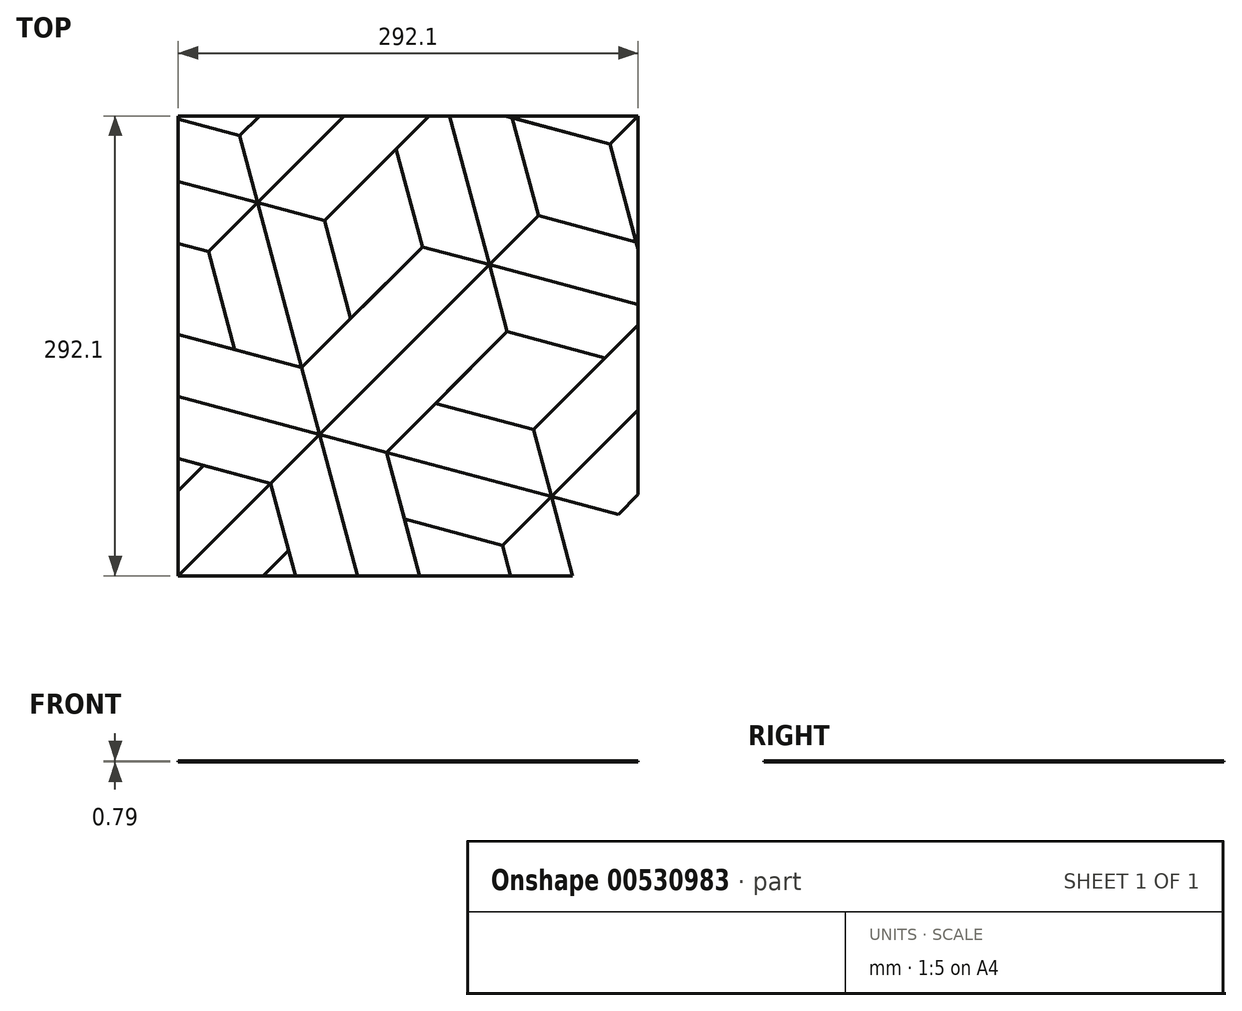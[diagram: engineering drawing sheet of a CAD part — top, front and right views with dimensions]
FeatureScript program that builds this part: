
annotation { "Feature Type Name" : "Feature", "Feature Type Description" : "" }
export const myFeature = defineFeature(function(context is Context, id is Id, definition is map)
    precondition{}
    {
        {
            var Q0;
            Q0=qCreatedBy(makeId("Top.planeOp"),FACE);
            var sketch = newSketch(context, id + "F0", { "sketchPlane" : qUnion([Q0])});
            skLineSegment(sketch, "E0.bottom", {"start": v(146.05, 146.05) * mm, "end": v(-146.05, 146.05) * mm});
            skLineSegment(sketch, "E0.top", {"start": v(146.05, -146.05) * mm, "end": v(-146.05, -146.05) * mm});
            skLineSegment(sketch, "E0.left", {"start": v(146.05, 146.05) * mm, "end": v(146.05, -146.05) * mm});
            skLineSegment(sketch, "E0.right", {"start": v(-146.05, 146.05) * mm, "end": v(-146.05, -146.05) * mm});
            skPoint(sketch, "E0.middle", {"position": v(0, 0) * mm});
            skLineSegment(sketch, "E1", {"start": v(-146.05, -146.05) * mm, "end": v(82.62, 82.62) * mm});
            skPoint(sketch, "E2", {"position": v(51.52, 51.52) * mm});
            skLineSegment(sketch, "E3", {"start": v(104.45, -146.05) * mm, "end": v(79.57, -53.2) * mm});
            skLineSegment(sketch, "E4", {"start": v(146.05, 26.19) * mm, "end": v(9.02, 62.9) * mm});
            skLineSegment(sketch, "E5", {"start": v(82.62, 82.62) * mm, "end": v(65.95, 144.84) * mm});
            skPoint(sketch, "E5.endSnap0", {"position": v(0, 146.05) * mm});
            skLineSegment(sketch, "E6", {"start": v(9.02, 62.9) * mm, "end": v(-7.65, 125.12) * mm});
            skLineSegment(sketch, "E7", {"start": v(82.62, 82.62) * mm, "end": v(144.84, 65.95) * mm});
            skLineSegment(sketch, "E8", {"start": v(62.9, 9.02) * mm, "end": v(125.12, -7.65) * mm});
            skLineSegment(sketch, "E9", {"start": v(62.9, 9.02) * mm, "end": v(-13.75, -67.63) * mm});
            skLineSegment(sketch, "E10", {"start": v(9.02, 62.9) * mm, "end": v(-67.63, -13.75) * mm});
            skPoint(sketch, "E11", {"position": v(-95.7, 90.96) * mm});
            skLineSegment(sketch, "E12", {"start": v(-107.08, 133.45) * mm, "end": v(-32.18, -146.05) * mm});
            skLineSegment(sketch, "E13", {"start": v(-126.8, 59.85) * mm, "end": v(-40.6, 146.05) * mm});
            skLineSegment(sketch, "E14", {"start": v(-53.2, 79.57) * mm, "end": v(-36.53, 17.36) * mm});
            skLineSegment(sketch, "E15", {"start": v(-53.2, 79.57) * mm, "end": v(13.28, 146.05) * mm});
            skLineSegment(sketch, "E16", {"start": v(-126.8, 59.85) * mm, "end": v(-110.13, -2.37) * mm});
            skLineSegment(sketch, "E17", {"start": v(-126.8, 59.85) * mm, "end": v(-146.05, 65) * mm});
            skLineSegment(sketch, "E18", {"start": v(-107.08, 133.45) * mm, "end": v(-94.48, 146.05) * mm});
            skLineSegment(sketch, "E19", {"start": v(-107.08, 133.45) * mm, "end": v(-146.05, 143.9) * mm});
            skLineSegment(sketch, "E20", {"start": v(-146.05, -32.18) * mm, "end": v(133.45, -107.08) * mm});
            skPoint(sketch, "E21", {"position": v(-13.75, -67.63) * mm});
            skLineSegment(sketch, "E22", {"start": v(-146.05, 7.26) * mm, "end": v(-67.63, -13.75) * mm});
            skLineSegment(sketch, "E23", {"start": v(-146.05, -71.63) * mm, "end": v(-87.36, -87.36) * mm});
            skLineSegment(sketch, "E24", {"start": v(59.85, -126.8) * mm, "end": v(146.05, -40.6) * mm});
            skLineSegment(sketch, "E25", {"start": v(79.57, -53.2) * mm, "end": v(146.05, 13.28) * mm});
            skLineSegment(sketch, "E26", {"start": v(59.85, -126.8) * mm, "end": v(65, -146.05) * mm});
            skLineSegment(sketch, "E27", {"start": v(133.45, -107.08) * mm, "end": v(143.9, -146.05) * mm});
            skLineSegment(sketch, "E28", {"start": v(143.9, -146.05) * mm, "end": v(133.45, -107.08) * mm});
            skLineSegment(sketch, "E29", {"start": v(133.45, -107.08) * mm, "end": v(146.05, -94.48) * mm});
            skLineSegment(sketch, "E30.trimOffspring", {"start": v(-13.75, -67.63) * mm, "end": v(7.26, -146.05) * mm});
            skLineSegment(sketch, "E31.trimOffspring", {"start": v(17.36, -36.53) * mm, "end": v(79.57, -53.2) * mm});
            skLineSegment(sketch, "E32.trimOffspring", {"start": v(-75.97, -129.85) * mm, "end": v(-92.17, -146.05) * mm});
            skLineSegment(sketch, "E33.trimOffspring", {"start": v(-2.37, -110.13) * mm, "end": v(59.85, -126.8) * mm});
            skLineSegment(sketch, "E34.trimOffspring", {"start": v(-129.85, -75.97) * mm, "end": v(-146.05, -92.17) * mm});
            skLineSegment(sketch, "E35.trimOffspring", {"start": v(-87.36, -87.36) * mm, "end": v(-71.63, -146.05) * mm});
            skLineSegment(sketch, "E36.trimOffspring", {"start": v(-53.2, 79.57) * mm, "end": v(-146.05, 104.45) * mm});
            skLineSegment(sketch, "E37.trimOffspring", {"start": v(62.9, 9.02) * mm, "end": v(26.19, 146.05) * mm});
            skLineSegment(sketch, "E38", {"start": v(61.44, 146.05) * mm, "end": v(128.17, 128.17) * mm});
            skLineSegment(sketch, "E39", {"start": v(128.17, 128.17) * mm, "end": v(146.05, 61.44) * mm});
            skLineSegment(sketch, "E40.trimOffspring", {"start": v(128.17, 128.17) * mm, "end": v(146.05, 146.05) * mm});
            skPoint(sketch, "E41.orphan", {"position": v(65.63, 146.05) * mm});
            skSolve(sketch);
        }
        {
            var Q0;
            {var subQ2=sQuery(id+"F0.wireOp",EDGE,"E0.bottom");var subQ6=sQuery(id+"F0.wireOp",EDGE,"E13");var subQ7=makeQuery(id+"F0.imprint","INTERSECT",VERTEX,{"derivedFrom":[subQ2,subQ6]});Q0=makeQuery(id+"F0.imprint","IMPRINT",FACE,{"disambiguationData":[TD([[makeQuery(id+"F0.imprint","IMPRINT",EDGE,{"disambiguationData":[TD([[subQ7,1.0]])],"derivedFrom":subQ2}),1.0]])]});}
            var Q1;
            {var subQ5=sQuery(id+"F0.wireOp",EDGE,"E16");Q1=makeQuery(id+"F0.imprint","IMPRINT",FACE,{"disambiguationData":[TD([[makeQuery(id+"F0.imprint","IMPRINT",EDGE,{"derivedFrom":subQ5}),1.0]])]});}
            var Q2;
            {var subQ0=sQuery(id+"F0.wireOp",EDGE,"E19");Q2=makeQuery(id+"F0.imprint","IMPRINT",FACE,{"disambiguationData":[TD([[makeQuery(id+"F0.imprint","IMPRINT",EDGE,{"derivedFrom":subQ0}),1.0]])]});}
            var Q3;
            {var subQ3=sQuery(id+"F0.wireOp",EDGE,"E32.trimOffspring");Q3=makeQuery(id+"F0.imprint","IMPRINT",FACE,{"disambiguationData":[TD([[makeQuery(id+"F0.imprint","IMPRINT",EDGE,{"derivedFrom":subQ3}),-1.0]])]});}
            var Q4;
            {var subQ0=sQuery(id+"F0.wireOp",EDGE,"E31.trimOffspring");Q4=makeQuery(id+"F0.imprint","IMPRINT",FACE,{"disambiguationData":[TD([[makeQuery(id+"F0.imprint","IMPRINT",EDGE,{"derivedFrom":subQ0}),-1.0]])]});}
            var Q5;
            {var subQ3=sQuery(id+"F0.wireOp",EDGE,"E29");Q5=makeQuery(id+"F0.imprint","IMPRINT",FACE,{"disambiguationData":[TD([[makeQuery(id+"F0.imprint","IMPRINT",EDGE,{"derivedFrom":subQ3}),1.0]])]});}
            var Q6;
            {var subQ3=sQuery(id+"F0.wireOp",EDGE,"E26");Q6=makeQuery(id+"F0.imprint","IMPRINT",FACE,{"disambiguationData":[TD([[makeQuery(id+"F0.imprint","IMPRINT",EDGE,{"derivedFrom":subQ3}),1.0]])]});}
            var Q7;
            {var subQ1=sQuery(id+"F0.wireOp",EDGE,"E10");var subQ3=makeQuery(id+"F0.imprint","INTERSECT",VERTEX,{"derivedFrom":[subQ1,sQuery(id+"F0.wireOp",EDGE,"E14")]});Q7=makeQuery(id+"F0.imprint","IMPRINT",FACE,{"disambiguationData":[TD([[makeQuery(id+"F0.imprint","IMPRINT",EDGE,{"disambiguationData":[TD([[subQ3,1.0]])],"derivedFrom":subQ1}),1.0]])]});}
            var Q8;
            {var subQ3=sQuery(id+"F0.wireOp",EDGE,"E12");var subQ5=sQuery(id+"F0.wireOp",EDGE,"E0.top");var subQ6=makeQuery(id+"F0.imprint","INTERSECT",VERTEX,{"derivedFrom":[subQ5,subQ3]});Q8=makeQuery(id+"F0.imprint","IMPRINT",FACE,{"disambiguationData":[TD([[makeQuery(id+"F0.imprint","IMPRINT",EDGE,{"disambiguationData":[TD([[subQ6,1.0]])],"derivedFrom":subQ5}),-1.0]])]});}
            var Q9;
            {var subQ1=sQuery(id+"F0.wireOp",EDGE,"E0.right");var subQ4=sQuery(id+"F0.wireOp",EDGE,"E20");var subQ5=makeQuery(id+"F0.imprint","INTERSECT",VERTEX,{"derivedFrom":[subQ1,subQ4]});Q9=makeQuery(id+"F0.imprint","IMPRINT",FACE,{"disambiguationData":[TD([[makeQuery(id+"F0.imprint","IMPRINT",EDGE,{"disambiguationData":[TD([[subQ5,-1.0]])],"derivedFrom":subQ1}),1.0]])]});}
            var Q10;
            {var subQ1=sQuery(id+"F0.wireOp",EDGE,"E8");Q10=makeQuery(id+"F0.imprint","IMPRINT",FACE,{"disambiguationData":[TD([[makeQuery(id+"F0.imprint","IMPRINT",EDGE,{"derivedFrom":subQ1}),1.0]])]});}
            var Q11;
            {var subQ5=sQuery(id+"F0.wireOp",EDGE,"E5");Q11=makeQuery(id+"F0.imprint","IMPRINT",FACE,{"disambiguationData":[TD([[makeQuery(id+"F0.imprint","IMPRINT",EDGE,{"derivedFrom":subQ5}),1.0]])]});}
            var Q12;
            {var subQ0=sQuery(id+"F0.wireOp",EDGE,"E40.trimOffspring");Q12=makeQuery(id+"F0.imprint","IMPRINT",FACE,{"disambiguationData":[TD([[makeQuery(id+"F0.imprint","IMPRINT",EDGE,{"derivedFrom":subQ0}),-1.0]])]});}
            extrude(context, id + "F1", {"entities" : qUnion([Q0, Q1, Q2, Q3, Q4, Q5, Q6, Q7, Q8, Q9, Q10, Q11, Q12]), "depth" : 0.8 * mm, "offsetDistance" : 25.4 * mm});
        }
        {
            var Q0;
            {var subQ3=sQuery(id+"F0.wireOp",EDGE,"E18");Q0=makeQuery(id+"F0.imprint","IMPRINT",FACE,{"disambiguationData":[TD([[makeQuery(id+"F0.imprint","IMPRINT",EDGE,{"derivedFrom":subQ3}),-1.0]])]});}
            var Q1;
            {var subQ0=sQuery(id+"F0.wireOp",EDGE,"E17");Q1=makeQuery(id+"F0.imprint","IMPRINT",FACE,{"disambiguationData":[TD([[makeQuery(id+"F0.imprint","IMPRINT",EDGE,{"derivedFrom":subQ0}),-1.0]])]});}
            var Q2;
            {var subQ3=sQuery(id+"F0.wireOp",EDGE,"E14");Q2=makeQuery(id+"F0.imprint","IMPRINT",FACE,{"disambiguationData":[TD([[makeQuery(id+"F0.imprint","IMPRINT",EDGE,{"derivedFrom":subQ3}),-1.0]])]});}
            var Q3;
            {var subQ0=sQuery(id+"F0.wireOp",EDGE,"E20");var subQ1=sQuery(id+"F0.wireOp",EDGE,"E0.right");var subQ2=makeQuery(id+"F0.imprint","INTERSECT",VERTEX,{"derivedFrom":[subQ1,subQ0]});Q3=makeQuery(id+"F0.imprint","IMPRINT",FACE,{"disambiguationData":[TD([[makeQuery(id+"F0.imprint","IMPRINT",EDGE,{"disambiguationData":[TD([[subQ2,1.0]])],"derivedFrom":subQ1}),1.0]])]});}
            var Q4;
            {var subQ3=sQuery(id+"F0.wireOp",EDGE,"E34.trimOffspring");Q4=makeQuery(id+"F0.imprint","IMPRINT",FACE,{"disambiguationData":[TD([[makeQuery(id+"F0.imprint","IMPRINT",EDGE,{"derivedFrom":subQ3}),1.0]])]});}
            var Q5;
            {var subQ4=sQuery(id+"F0.wireOp",EDGE,"E12");var subQ5=sQuery(id+"F0.wireOp",EDGE,"E0.top");var subQ6=makeQuery(id+"F0.imprint","INTERSECT",VERTEX,{"derivedFrom":[subQ5,subQ4]});Q5=makeQuery(id+"F0.imprint","IMPRINT",FACE,{"disambiguationData":[TD([[makeQuery(id+"F0.imprint","IMPRINT",EDGE,{"disambiguationData":[TD([[subQ6,-1.0]])],"derivedFrom":subQ5}),-1.0]])]});}
            var Q6;
            {var subQ1=sQuery(id+"F0.wireOp",EDGE,"E9");var subQ5=makeQuery(id+"F0.imprint","INTERSECT",VERTEX,{"derivedFrom":[subQ1,sQuery(id+"F0.wireOp",EDGE,"E31.trimOffspring")]});Q6=makeQuery(id+"F0.imprint","IMPRINT",FACE,{"disambiguationData":[TD([[makeQuery(id+"F0.imprint","IMPRINT",EDGE,{"disambiguationData":[TD([[subQ5,1.0]])],"derivedFrom":subQ1}),-1.0]])]});}
            var Q7;
            {var subQ5=sQuery(id+"F0.wireOp",EDGE,"E33.trimOffspring");Q7=makeQuery(id+"F0.imprint","IMPRINT",FACE,{"disambiguationData":[TD([[makeQuery(id+"F0.imprint","IMPRINT",EDGE,{"derivedFrom":subQ5}),1.0]])]});}
            var Q8;
            {var subQ3=sQuery(id+"F0.wireOp",EDGE,"E28");Q8=makeQuery(id+"F0.imprint","IMPRINT",FACE,{"disambiguationData":[TD([[makeQuery(id+"F0.imprint","IMPRINT",EDGE,{"derivedFrom":subQ3}),1.0]])]});}
            var Q9;
            {var subQ0=sQuery(id+"F0.wireOp",EDGE,"E24");var subQ1=sQuery(id+"F0.wireOp",EDGE,"E0.left");var subQ2=makeQuery(id+"F0.imprint","INTERSECT",VERTEX,{"derivedFrom":[subQ1,subQ0]});Q9=makeQuery(id+"F0.imprint","IMPRINT",FACE,{"disambiguationData":[TD([[makeQuery(id+"F0.imprint","IMPRINT",EDGE,{"disambiguationData":[TD([[subQ2,1.0]])],"derivedFrom":subQ1}),-1.0]])]});}
            var Q10;
            {var subQ0=sQuery(id+"F0.wireOp",EDGE,"E7");Q10=makeQuery(id+"F0.imprint","IMPRINT",FACE,{"disambiguationData":[TD([[makeQuery(id+"F0.imprint","IMPRINT",EDGE,{"derivedFrom":subQ0}),-1.0]])]});}
            var Q11;
            {var subQ0=sQuery(id+"F0.wireOp",EDGE,"E6");Q11=makeQuery(id+"F0.imprint","IMPRINT",FACE,{"disambiguationData":[TD([[makeQuery(id+"F0.imprint","IMPRINT",EDGE,{"derivedFrom":subQ0}),-1.0]])]});}
            var Q12;
            {var subQ0=sQuery(id+"F0.wireOp",EDGE,"E40.trimOffspring");Q12=makeQuery(id+"F0.imprint","IMPRINT",FACE,{"disambiguationData":[TD([[makeQuery(id+"F0.imprint","IMPRINT",EDGE,{"derivedFrom":subQ0}),1.0]])]});}
            extrude(context, id + "F2", {"entities" : qUnion([Q0, Q1, Q2, Q3, Q4, Q5, Q6, Q7, Q8, Q9, Q10, Q11, Q12]), "depth" : 0.8 * mm, "offsetDistance" : 25.4 * mm});
        }
        {
            var Q0;
            {var subQ3=sQuery(id+"F0.wireOp",EDGE,"E18");Q0=makeQuery(id+"F0.imprint","IMPRINT",FACE,{"disambiguationData":[TD([[makeQuery(id+"F0.imprint","IMPRINT",EDGE,{"derivedFrom":subQ3}),1.0]])]});}
            var Q1;
            {var subQ4=sQuery(id+"F0.wireOp",EDGE,"E16");Q1=makeQuery(id+"F0.imprint","IMPRINT",FACE,{"disambiguationData":[TD([[makeQuery(id+"F0.imprint","IMPRINT",EDGE,{"derivedFrom":subQ4}),-1.0]])]});}
            var Q2;
            {var subQ0=sQuery(id+"F0.wireOp",EDGE,"E6");Q2=makeQuery(id+"F0.imprint","IMPRINT",FACE,{"disambiguationData":[TD([[makeQuery(id+"F0.imprint","IMPRINT",EDGE,{"derivedFrom":subQ0}),1.0]])]});}
            var Q3;
            {var subQ0=sQuery(id+"F0.wireOp",EDGE,"E5");Q3=makeQuery(id+"F0.imprint","IMPRINT",FACE,{"disambiguationData":[TD([[makeQuery(id+"F0.imprint","IMPRINT",EDGE,{"derivedFrom":subQ0}),-1.0]])]});}
            var Q4;
            {var subQ0=sQuery(id+"F0.wireOp",EDGE,"E8");Q4=makeQuery(id+"F0.imprint","IMPRINT",FACE,{"disambiguationData":[TD([[makeQuery(id+"F0.imprint","IMPRINT",EDGE,{"derivedFrom":subQ0}),-1.0]])]});}
            var Q5;
            {var subQ3=sQuery(id+"F0.wireOp",EDGE,"E28");Q5=makeQuery(id+"F0.imprint","IMPRINT",FACE,{"disambiguationData":[TD([[makeQuery(id+"F0.imprint","IMPRINT",EDGE,{"derivedFrom":subQ3}),-1.0]])]});}
            var Q6;
            {var subQ0=sQuery(id+"F0.wireOp",EDGE,"E26");Q6=makeQuery(id+"F0.imprint","IMPRINT",FACE,{"disambiguationData":[TD([[makeQuery(id+"F0.imprint","IMPRINT",EDGE,{"derivedFrom":subQ0}),-1.0]])]});}
            var Q7;
            {var subQ0=sQuery(id+"F0.wireOp",EDGE,"E32.trimOffspring");Q7=makeQuery(id+"F0.imprint","IMPRINT",FACE,{"disambiguationData":[TD([[makeQuery(id+"F0.imprint","IMPRINT",EDGE,{"derivedFrom":subQ0}),1.0]])]});}
            var Q8;
            {var subQ3=sQuery(id+"F0.wireOp",EDGE,"E34.trimOffspring");Q8=makeQuery(id+"F0.imprint","IMPRINT",FACE,{"disambiguationData":[TD([[makeQuery(id+"F0.imprint","IMPRINT",EDGE,{"derivedFrom":subQ3}),-1.0]])]});}
            extrude(context, id + "F3", {"entities" : qUnion([Q0, Q1, Q2, Q3, Q4, Q5, Q6, Q7, Q8]), "depth" : 0.8 * mm, "offsetDistance" : 25.4 * mm});
        }
    });
